# Revit family: BE-40_GENERADO
name_source: partatom
category: Equipos especializados
units: mm (PartAtom-declared; Revit-internal decimal feet)

## family parameters
Compartido = No
Corte con vacíos al cargar = No
Cota de conector redondo = Diámetro de uso
Número OmniClass = 23.21.21.31.11
Punto de cálculo de habitación = No
Se basa en plano de trabajo = No
Siempre vertical = Sí
Tipo de pieza = Normal

## types (7) — shared parameters
Fabricante = SAMMIC S.L.
Foodservice Equipment Identifier = Sí
Revision Code = 1
URL = https://www.sammic.com
URL Cutsheet = http://www.sammic.com
zero-valued in all types: Elevación por defecto

## per-type parameters (varying)
| type | Comentarios de tipo | Conn Plug | Cycle | Depth | Electric Connection Type | FL Amps | HP | Height | Modelo | Phase | Specification by Manufacturer | Volts | Watts | Weight in Pounds | Width |
| Food mixer BE-40 230/50-60/1 | Floorstanding unit with 40 lt./ qt. bowl. | EU (SCHUKO 2P+G) | 50 Hz | 777 mm  [stored 2.54921 ft] |  | 15 A | 1.88 | 1202 mm  [stored 3.94357 ft] | 1500240 | 1 | "C" models, complete with attachment drive for accessories.
"I" models with stainless steel column. | 230 V | 1400 W | 255.7 | 586 mm  [stored 1.92257 ft] |
| Food mixer BE-40I 230/50-60/1 | Floorstanding unit with 40 lt./ qt. bowl. | EU (SCHUKO 2P+G) | 50 Hz | 777 mm  [stored 2.54921 ft] |  | 15 A | 1.88 | 1202 mm  [stored 3.94357 ft] | 1500246 | 1 | "C" models, complete with attachment drive for accessories.
"I" models with stainless steel column. | 230 V | 1400 W | 273.4 | 586 mm  [stored 1.92257 ft] |
| Food mixer BE-40C 230/50-60/1 | Floorstanding unit with 40 lt./ qt. bowl. | EU (SCHUKO 2P+G) | 50 Hz | 777 mm  [stored 2.54921 ft] |  | 15 A | 1.88 | 1202 mm  [stored 3.94357 ft] | 1500241 | 1 | "C" models, complete with attachment drive for accessories.
"I" models with stainless steel column. | 230 V | 1400 W | 257.9 | 586 mm  [stored 1.92257 ft] |
| Food mixer BE-40 400-440/50-60/3 | Floorstanding unit with 40 lt./ qt. bowl.

ELECTRICAL DATA:

440V/50-60Hz/3~ (4.9A) |  | 50 Hz | 777 mm  [stored 2.54921 ft] | 3P+G | 5 A | 1.88 | 1202 mm  [stored 3.94357 ft] | 1500247 | 3 | "C" models, complete with attachment drive for accessories.
"I" models with stainless steel column. | 400 V | 1400 W | 260.1 | 586 mm  [stored 1.92257 ft] |
| Food mixer BE-40C 400-440/50-60/3 | Floorstanding unit with 40 lt./ qt. bowl.

ELECTRICAL DATA:

440V/50-60Hz/3~ (4.9A) |  | 50 Hz | 777 mm  [stored 2.54921 ft] | 3P+G | 5 A | 1.88 | 1202 mm  [stored 3.94357 ft] | 1500248 | 3 | "C" models, complete with attachment drive for accessories.
"I" models with stainless steel column. | 400 V | 1400 W | 262.4 | 586 mm  [stored 1.92257 ft] |
| Food mixer BE-40 208-240/50-60/1 | Floorstanding unit with 40 lt./ qt. bowl.

ELECTRICAL DATA:

240V/50-60Hz/1~ (14.8A) | USA (NEMA 6-20P / 2P) | 50 Hz | 777 mm  [stored 2.54921 ft] |  | 15 A | 1.88 | 1202 mm  [stored 3.94357 ft] | 1500249 | 1 | "C" models, complete with attachment drive for accessories.
"I" models with stainless steel column. | 208 V | 1400 W | 260.1 | 586 mm  [stored 1.92257 ft] |
| External loader BE-20/30/40 |  |  | 0 Hz | 0 mm  [stored 0 ft] |  | 0 A |  | 0 mm  [stored 0 ft] | 2509612 | 0 |  | 0 V | 0 W | 0 | 0 mm  [stored 0 ft] |

note: column(s) folded — value = type name in every type: Descripción

note: [stored X ft] marks values corroborated as IEEE doubles in the binary element streams (Revit-internal decimal feet)
